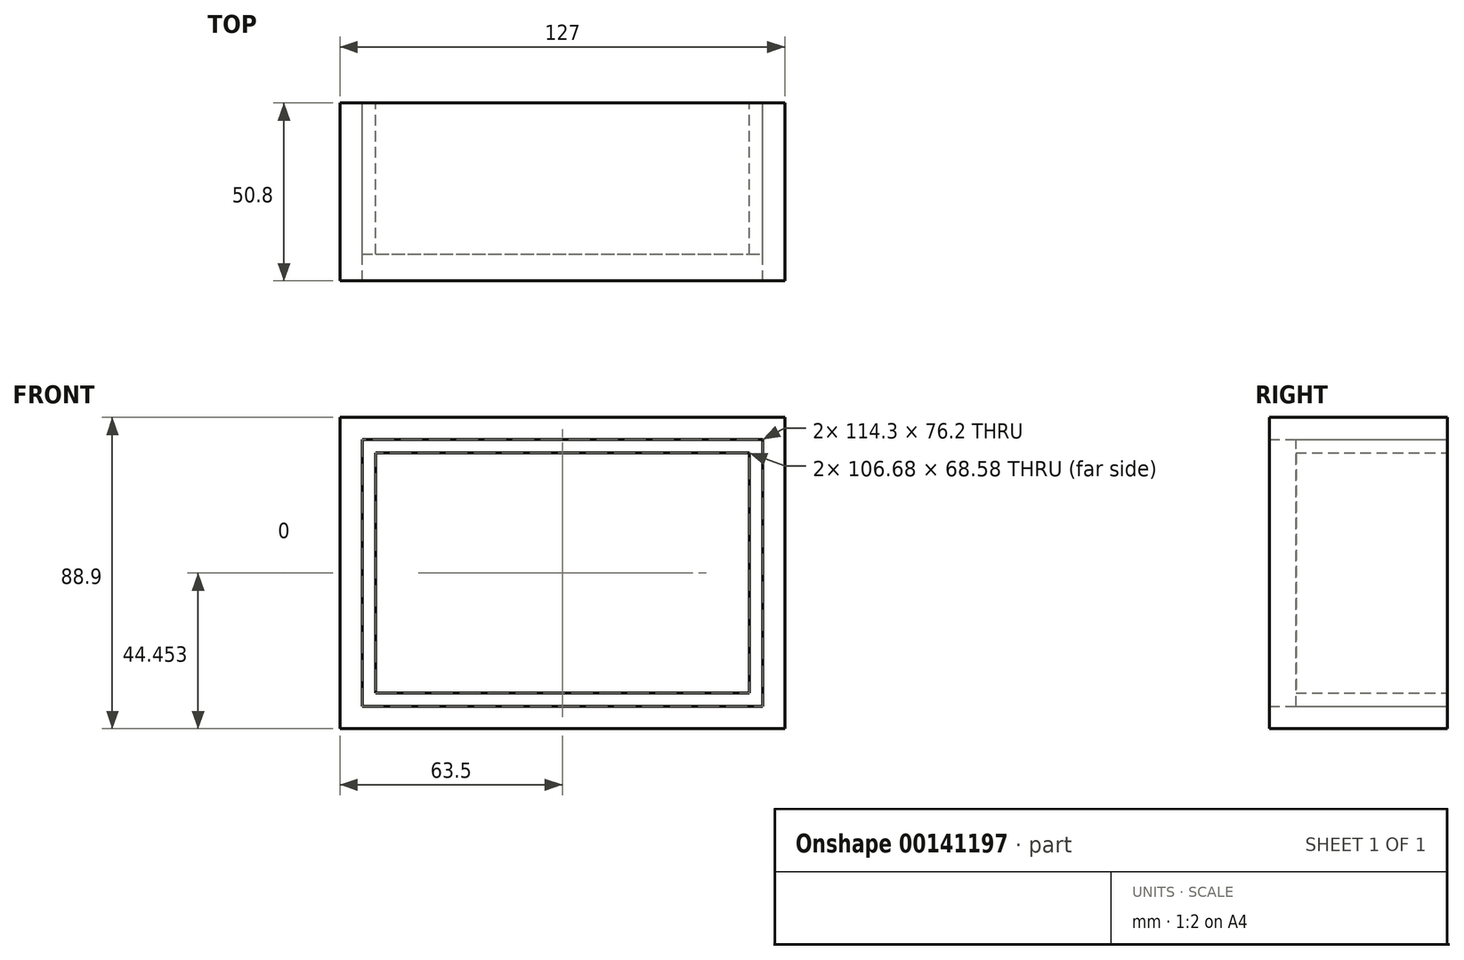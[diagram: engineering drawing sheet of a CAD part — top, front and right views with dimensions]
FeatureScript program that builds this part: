
annotation { "Feature Type Name" : "Feature", "Feature Type Description" : "" }
export const myFeature = defineFeature(function(context is Context, id is Id, definition is map)
    precondition{}
    {
        {
            var Q0;
            Q0=qCreatedBy(makeId("Front.planeOp"),FACE);
            var sketch = newSketch(context, id + "F0", { "sketchPlane" : qUnion([Q0])});
            skLineSegment(sketch, "E0.bottom", {"start": v(59.1, 34.96) * mm, "end": v(-67.9, 34.96) * mm});
            skLineSegment(sketch, "E0.top", {"start": v(59.1, -53.94) * mm, "end": v(-67.9, -53.94) * mm});
            skLineSegment(sketch, "E0.left", {"start": v(59.1, 34.96) * mm, "end": v(59.1, -53.94) * mm});
            skLineSegment(sketch, "E0.right", {"start": v(-67.9, 34.96) * mm, "end": v(-67.9, -53.94) * mm});
            skLineSegment(sketch, "E1.bottom", {"start": v(-61.55, -47.59) * mm, "end": v(52.75, -47.59) * mm});
            skLineSegment(sketch, "E1.top", {"start": v(-61.55, 28.61) * mm, "end": v(52.75, 28.61) * mm});
            skLineSegment(sketch, "E1.left", {"start": v(-61.55, -47.59) * mm, "end": v(-61.55, 28.61) * mm});
            skLineSegment(sketch, "E1.right", {"start": v(52.75, -47.59) * mm, "end": v(52.75, 28.61) * mm});
            skLineSegment(sketch, "E2.bottom", {"start": v(-57.74, 24.8) * mm, "end": v(48.94, 24.8) * mm});
            skLineSegment(sketch, "E2.top", {"start": v(-57.74, -43.78) * mm, "end": v(48.94, -43.78) * mm});
            skLineSegment(sketch, "E2.left", {"start": v(-57.74, 24.8) * mm, "end": v(-57.74, -43.78) * mm});
            skLineSegment(sketch, "E2.right", {"start": v(48.94, 24.8) * mm, "end": v(48.94, -43.78) * mm});
            skSolve(sketch);
        }
        {
            var Q0;
            Q0=makeQuery(id+"F0.imprint","IMPRINT",FACE,{"disambiguationData":[TD([[makeQuery(id+"F0.imprint","IMPRINT",EDGE,{"derivedFrom":sQuery(id+"F0.wireOp",EDGE,"E1.bottom")}),1.0]])]});
            extrude(context, id + "F1", {"entities" : qUnion([Q0]), "depth" : 43.18 * mm});
        }
        {
            var Q0;
            Q0=makeQuery(id+"F0.imprint","IMPRINT",FACE,{"disambiguationData":[TD([[makeQuery(id+"F0.imprint","IMPRINT",EDGE,{"derivedFrom":sQuery(id+"F0.wireOp",EDGE,"E0.bottom")}),1.0]])]});
            extrude(context, id + "F2", {"entities" : qUnion([Q0]), "depth" : 50.8 * mm});
        }
    });
